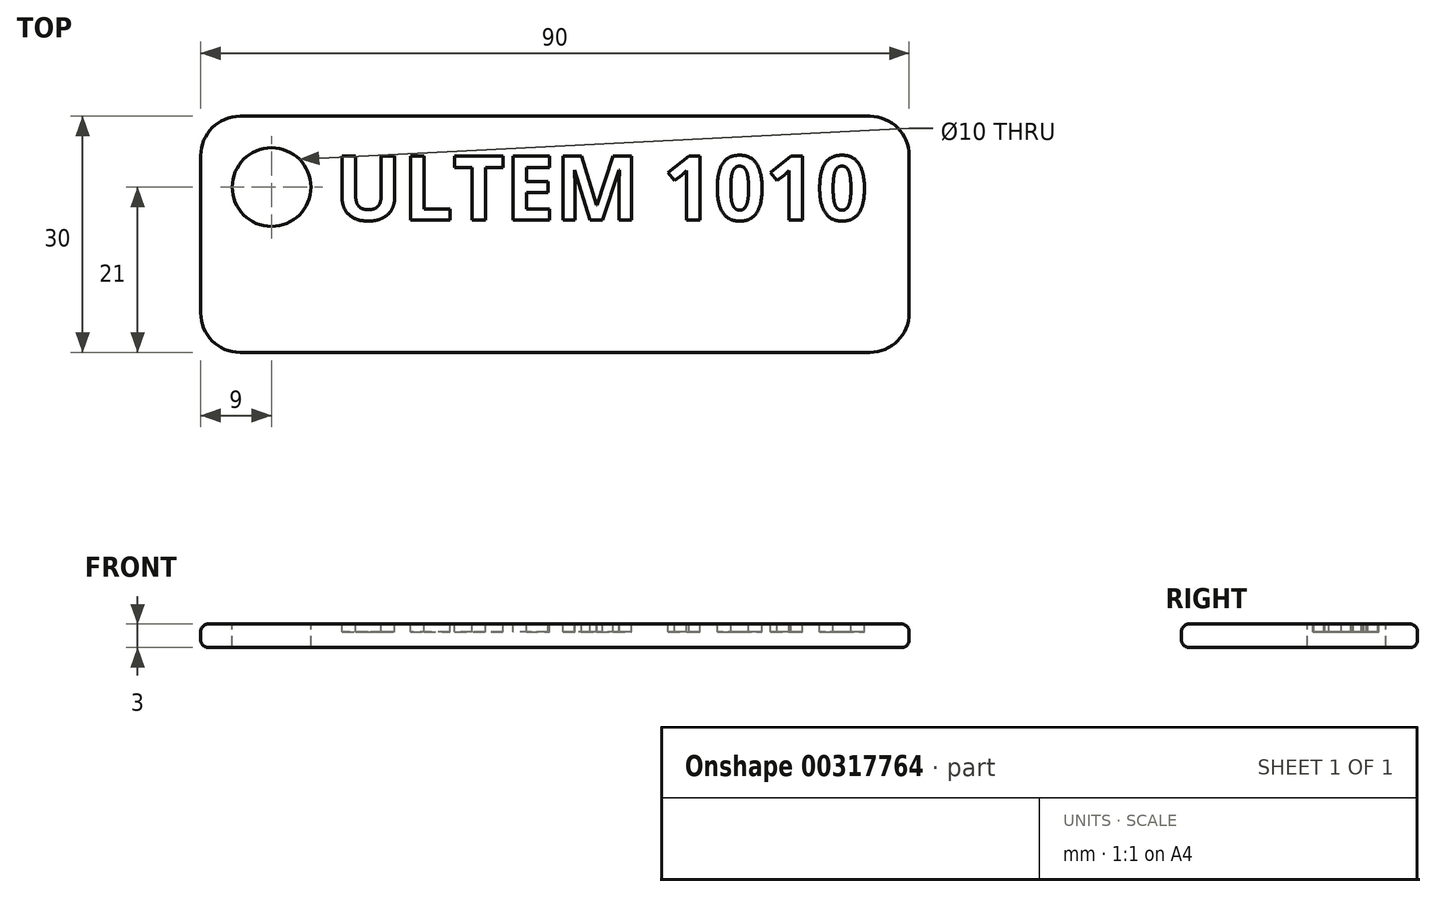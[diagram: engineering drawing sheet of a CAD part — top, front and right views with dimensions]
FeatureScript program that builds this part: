
annotation { "Feature Type Name" : "Feature", "Feature Type Description" : "" }
export const myFeature = defineFeature(function(context is Context, id is Id, definition is map)
    precondition{}
    {
        {
            var Q0;
            Q0=qCreatedBy(makeId("Top.planeOp"),FACE);
            var sketch = newSketch(context, id + "F0", { "sketchPlane" : qUnion([Q0])});
            skLineSegment(sketch, "E0.bottom", {"start": v(-45, 15) * mm, "end": v(45, 15) * mm});
            skLineSegment(sketch, "E0.top", {"start": v(-45, -15) * mm, "end": v(45, -15) * mm});
            skLineSegment(sketch, "E0.left", {"start": v(-45, 15) * mm, "end": v(-45, -15) * mm});
            skLineSegment(sketch, "E0.right", {"start": v(45, 15) * mm, "end": v(45, -15) * mm});
            skLineSegment(sketch, "E1", {"start": v(-45, 15) * mm, "end": v(45, -15) * mm, "construction": true});
            skSolve(sketch);
        }
        {
            var Q0;
            Q0=makeQuery(id+"F0.imprint","IMPRINT",FACE,{"disambiguationData":[TD([[makeQuery(id+"F0.imprint","IMPRINT",EDGE,{"derivedFrom":sQuery(id+"F0.wireOp",EDGE,"E0.bottom")}),-1.0]])]});
            extrude(context, id + "F1", {"entities" : qUnion([Q0]), "depth" : 3 * mm});
        }
        {
            var Q0;
            Q0=makeQuery(id+"F1.opExtrude","CAP_FACE",FACE,{"disambiguationData":[OSD([sQuery(id+"F0.wireOp",EDGE,"E0.bottom"),sQuery(id+"F0.wireOp",EDGE,"E0.top"),sQuery(id+"F0.wireOp",EDGE,"E0.left"),sQuery(id+"F0.wireOp",EDGE,"E0.right")])],"isStart":false});
            var Q1;
            Q1=makeQuery(id+"F1.opExtrude","CAP_FACE",FACE,{"disambiguationData":[OSD([sQuery(id+"F0.wireOp",EDGE,"E0.bottom"),sQuery(id+"F0.wireOp",EDGE,"E0.top"),sQuery(id+"F0.wireOp",EDGE,"E0.left"),sQuery(id+"F0.wireOp",EDGE,"E0.right")])],"isStart":true});
            fillet(context, id + "F2", {"entities" : qUnion([Q0, Q1]), "radius" : 1 * mm, "tangentPropagation" : true, "allowEdgeOverflow" : false});
        }
        {
            var Q0;
            Q0=makeQuery(id+"F1.opExtrude","SWEPT_EDGE",EDGE,{"disambiguationData":[OSD([sQuery(id+"F0.wireOp",EDGE,"E0.top"),sQuery(id+"F0.wireOp",EDGE,"E0.right")])]});
            var Q1;
            Q1=makeQuery(id+"F1.opExtrude","SWEPT_EDGE",EDGE,{"disambiguationData":[OSD([sQuery(id+"F0.wireOp",EDGE,"E0.bottom"),sQuery(id+"F0.wireOp",EDGE,"E0.right")])]});
            var Q2;
            Q2=makeQuery(id+"F1.opExtrude","SWEPT_EDGE",EDGE,{"disambiguationData":[OSD([sQuery(id+"F0.wireOp",EDGE,"E0.bottom"),sQuery(id+"F0.wireOp",EDGE,"E0.left")])]});
            var Q3;
            Q3=makeQuery(id+"F1.opExtrude","SWEPT_EDGE",EDGE,{"disambiguationData":[OSD([sQuery(id+"F0.wireOp",EDGE,"E0.top"),sQuery(id+"F0.wireOp",EDGE,"E0.left")])]});
            fillet(context, id + "F3", {"entities" : qUnion([Q0, Q1, Q2, Q3]), "radius" : 5 * mm, "tangentPropagation" : true, "allowEdgeOverflow" : false});
        }
        {
            var Q0;
            {var subQ0=sQuery(id+"F0.wireOp",EDGE,"E0.left");var subQ2=sQuery(id+"F0.wireOp",EDGE,"E0.bottom");var subQ4=sQuery(id+"F0.wireOp",EDGE,"E0.right");var subQ6=sQuery(id+"F0.wireOp",EDGE,"E0.top");Q0=makeQuery(id+"FmQCBBX3Ub0qneL_1.boolean.opBoolean","SPLIT",FACE,{"disambiguationData":[TD([makeQuery(id+"FmQCBBX3Ub0qneL_1.opExtrude","SWEPT_FACE",FACE,{"disambiguationData":[OSD([sQuery(id+"FOCoeRmDbjhRCuz_1.wireOp",EDGE,"4a1fb44a-e7be-4e23-9449-000d953c446c.sketch_text.stroke-0")])]})])],"derivedFrom":makeQuery(id+"F1.opExtrude","CAP_FACE",FACE,{"disambiguationData":[OSD([subQ2,subQ6,subQ0,subQ4])],"isStart":false})});}
            var sketch = newSketch(context, id + "F4", { "sketchPlane" : qUnion([Q0])});
            skCircle(sketch, "E2", {"center": v(-36, 6) * mm, "radius": 5 * mm});
            skSolve(sketch);
        }
        {
            var Q0;
            Q0=qSketchRegion(id+"F4",true);
            extrude(context, id + "F5", {"entities" : qUnion([Q0]), "operationType" : NewBodyOperationType.REMOVE, "oppositeDirection" : true, "depth" : 3 * mm});
        }
        {
            var Q0;
            Q0=makeQuery(id+"F1.opExtrude","CAP_FACE",FACE,{"disambiguationData":[OSD([sQuery(id+"F0.wireOp",EDGE,"E0.bottom"),sQuery(id+"F0.wireOp",EDGE,"E0.top"),sQuery(id+"F0.wireOp",EDGE,"E0.left"),sQuery(id+"F0.wireOp",EDGE,"E0.right")])],"isStart":false});
            var sketch = newSketch(context, id + "F6", { "sketchPlane" : qUnion([Q0])});
            skText(sketch, "E3", { "text": "ULTEM 1010", "fontName": "OpenSans-Bold.ttf"});
            const initialGuessF6  = {"E3": [-0.028, 0.0018, 1, 0, 0.0082]};
            skSetInitialGuess(sketch, initialGuessF6);
            skSolve(sketch);
        }
        {
            var Q0;
            Q0=qSketchRegion(id+"F6",true);
            extrude(context, id + "F7", {"entities" : qUnion([Q0]), "operationType" : NewBodyOperationType.REMOVE, "oppositeDirection" : true, "depth" : 1 * mm});
        }
    });
